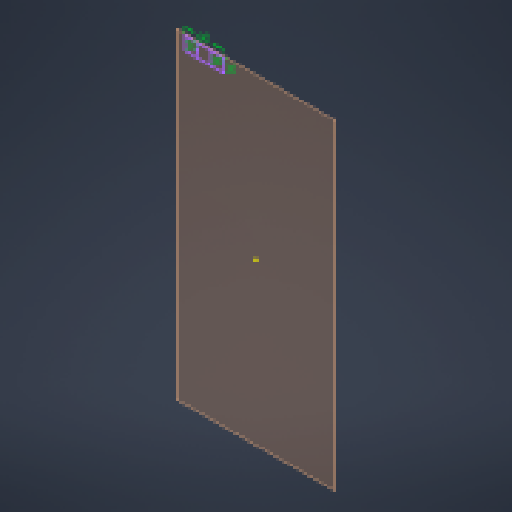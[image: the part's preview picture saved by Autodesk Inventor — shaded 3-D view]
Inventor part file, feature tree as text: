
AUTODESK INVENTOR PART (.ipt)
format: ipt  version: 2024 (Build 280153000, 153)  size: 119,808 bytes
history: native  units: mm
features: other x4, plane x1, sketch x1
ambient origin geometry x8: Origin, YZ Plane, XZ Plane, XY Plane, X Axis, Y Axis, Z Axis, Center Point
feature tree (6):
  plane  "Plano de trabajo1"
  sketch  "Boceto1"  dims[d0=90.0mm d1=30.0mm d2=30.0mm d3=30.0mm]
  other  "<userpath>\Downloads\Piezas CMR\Marco_APM_001\Marco_apm_001-1.iam"
  other  "Marco_apm_001-1.iam"
  other  "Marco_Conveyor_Aereo:1"
  other  "Marco:1"
